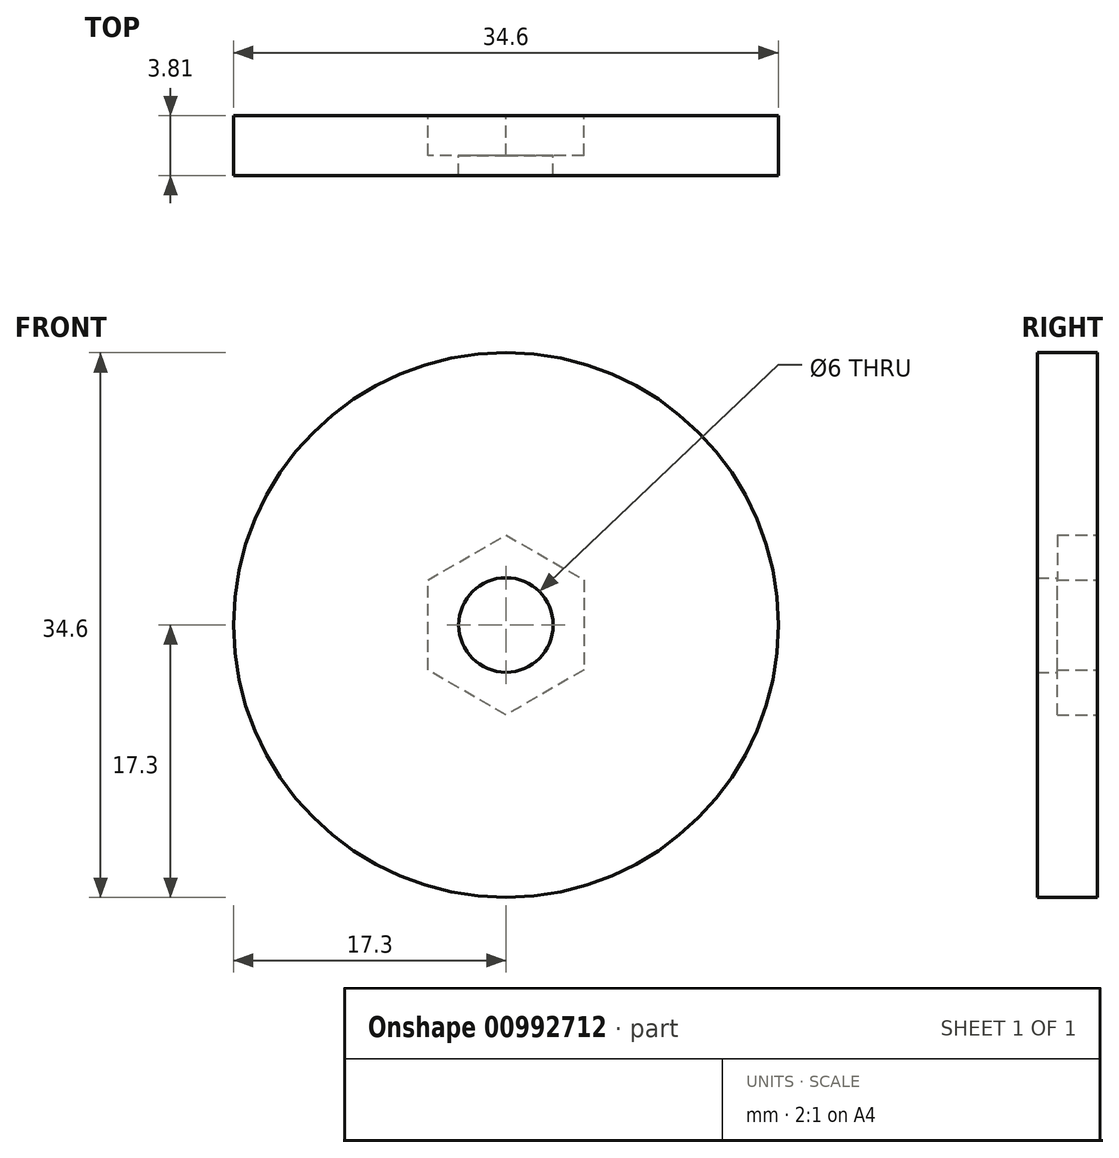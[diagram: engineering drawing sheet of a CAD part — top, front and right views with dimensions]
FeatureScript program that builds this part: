
annotation { "Feature Type Name" : "Feature", "Feature Type Description" : "" }
export const myFeature = defineFeature(function(context is Context, id is Id, definition is map)
    precondition{}
    {
        {
            var Q0;
            Q0=qCreatedBy(makeId("Front.planeOp"),FACE);
            var sketch = newSketch(context, id + "F0", { "sketchPlane" : qUnion([Q0])});
            skCircle(sketch, "E0", {"center": v(0, 0) * mm, "radius": 17.3 * mm});
            skSolve(sketch);
        }
        {
            var Q0;
            Q0=qSketchRegion(id+"F0",true);
            extrude(context, id + "F1", {"entities" : qUnion([Q0]), "depth" : 3.8 * mm, "offsetDistance" : 25.4 * mm});
        }
        {
            var Q0;
            Q0=qCreatedBy(makeId("Front.planeOp"),FACE);
            var sketch = newSketch(context, id + "F2", { "sketchPlane" : qUnion([Q0])});
            skCircle(sketch, "E1.cCircle", {"center": v(0, 0) * mm, "radius": 4.95 * mm, "construction": true});
            skLineSegment(sketch, "E1.0", {"start": v(-4.95, -2.86) * mm, "end": v(-4.95, 2.86) * mm});
            skLineSegment(sketch, "E1.1", {"start": v(-4.95, 2.86) * mm, "end": v(0, 5.72) * mm});
            skLineSegment(sketch, "E1.2", {"start": v(0, 5.72) * mm, "end": v(4.95, 2.86) * mm});
            skLineSegment(sketch, "E1.3", {"start": v(4.95, 2.86) * mm, "end": v(4.95, -2.86) * mm});
            skLineSegment(sketch, "E1.4", {"start": v(4.95, -2.86) * mm, "end": v(0, -5.72) * mm});
            skLineSegment(sketch, "E1.5", {"start": v(0, -5.72) * mm, "end": v(-4.95, -2.86) * mm});
            skPoint(sketch, "E1.0.midPoint", {"position": v(-4.95, 0) * mm});
            skSolve(sketch);
        }
        {
            var Q0;
            Q0=qSketchRegion(id+"F2",true);
            extrude(context, id + "F3", {"entities" : qUnion([Q0]), "operationType" : NewBodyOperationType.REMOVE, "depth" : 1.27 * mm, "offsetDistance" : 25.4 * mm});
        }
        {
            var Q0;
            Q0=qSketchRegion(id+"F2",true);
            extrude(context, id + "F4", {"entities" : qUnion([Q0]), "operationType" : NewBodyOperationType.REMOVE, "depth" : 2.54 * mm, "offsetDistance" : 25.4 * mm});
        }
        {
            var Q0;
            Q0=makeQuery(id+"F1.opExtrude","CAP_FACE",FACE,{"disambiguationData":[OSD([sQuery(id+"F0.wireOp",EDGE,"E0")])],"isStart":true});
            var sketch = newSketch(context, id + "F5", { "sketchPlane" : qUnion([Q0])});
            skCircle(sketch, "E2", {"center": v(0, 0) * mm, "radius": 3 * mm});
            skSolve(sketch);
        }
        {
            var Q0;
            Q0=qSketchRegion(id+"F5",true);
            extrude(context, id + "F6", {"entities" : qUnion([Q0]), "operationType" : NewBodyOperationType.REMOVE, "endBound" : BoundingType.THROUGH_ALL, "oppositeDirection" : true, "depth" : 25.4 * mm, "offsetDistance" : 25.4 * mm});
        }
    });
